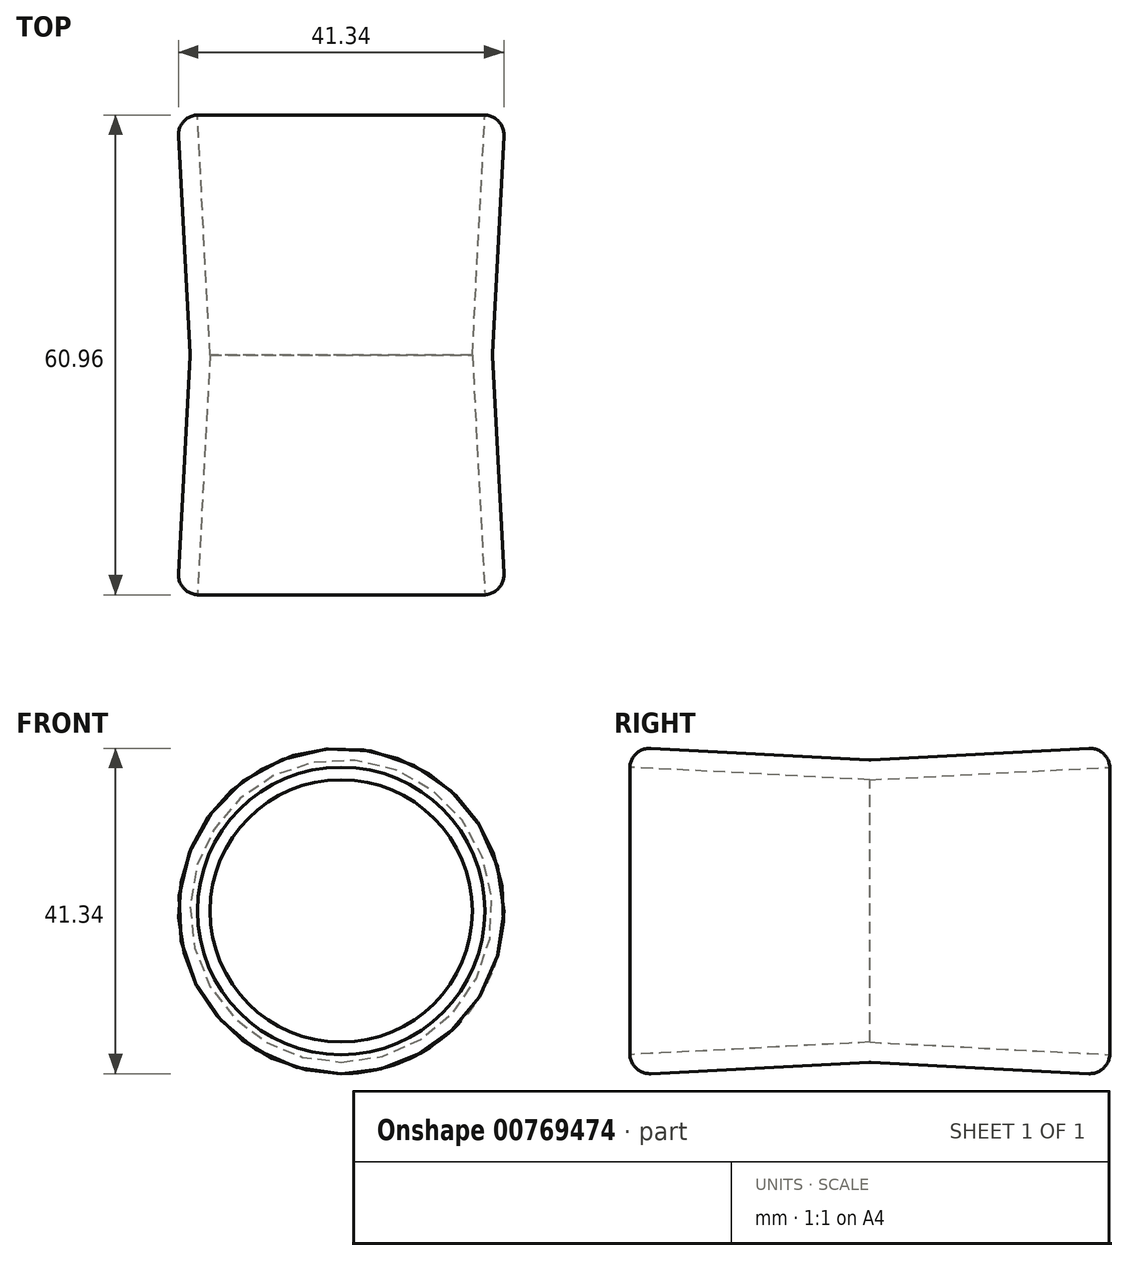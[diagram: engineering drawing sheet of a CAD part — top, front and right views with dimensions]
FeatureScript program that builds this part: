
annotation { "Feature Type Name" : "Feature", "Feature Type Description" : "" }
export const myFeature = defineFeature(function(context is Context, id is Id, definition is map)
    precondition{}
    {
        {
            var Q0;
            Q0=qCreatedBy(makeId("Front.planeOp"),FACE);
            var sketch = newSketch(context, id + "F0", { "sketchPlane" : qUnion([Q0])});
            skCircle(sketch, "E0", {"center": v(0, 0) * mm, "radius": 19.2 * mm});
            skSolve(sketch);
        }
        {
            var Q0;
            Q0 = qSketchRegion(id + "F0", true);
            extrude(context, id + "F1", {"entities" : qUnion([Q0]), "depth" : 30.48 * mm, "offsetDistance" : 25.4 * mm, "hasDraft" : true, "draftAngle" : 3 * degree, "hasSecondDirection" : true, "secondDirectionOppositeDirection" : true, "secondDirectionDepth" : 30.48 * mm, "hasSecondDirectionDraft" : true, "secondDirectionDraftAngle" : 3 * degree});
        }
        {
            var Q0;
            Q0=makeQuery(id+"F1.opExtrude","CAP_FACE",FACE,{"disambiguationData":[OSD([sQuery(id+"F0.wireOp",EDGE,"E0")])],"isStart":false});
            var Q1;
            Q1=makeQuery(id+"F1.opExtrude","CAP_FACE",FACE,{"disambiguationData":[OSD([sQuery(id+"F0.wireOp",EDGE,"E0")])],"isStart":true});
            shell(context, id + "F2", {"entities" : qUnion([Q0, Q1]), "thickness" : 2.54 * mm});
        }
        {
            var Q0;
            Q0=makeQuery(id+"F1.*.split.splitOp","SPLIT",FACE,{"derivedFrom":makeQuery(id+"F1.opExtrude","SWEPT_FACE",FACE,{"disambiguationData":[OSD([sQuery(id+"F0.wireOp",EDGE,"E0")])]}),"isFromBackBody":true});
            var Q1;
            Q1=makeQuery(id+"F1.*.split.splitOp","SPLIT",FACE,{"derivedFrom":makeQuery(id+"F1.opExtrude","SWEPT_FACE",FACE,{"disambiguationData":[OSD([sQuery(id+"F0.wireOp",EDGE,"E0")])]})});
            fillet(context, id + "F3", {"entities" : qUnion([Q0, Q1]), "radius" : 2.54 * mm, "tangentPropagation" : true, "allowEdgeOverflow" : false});
        }
    });
